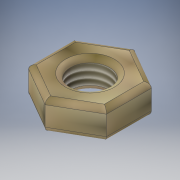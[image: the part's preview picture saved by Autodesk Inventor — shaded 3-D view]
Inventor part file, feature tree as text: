
AUTODESK INVENTOR PART (.ipt)
format: ipt  version: 2019 (Build 230136000, 136)  size: 160,768 bytes
history: native  units: mm
features: extrude x1, fillet x1, thread x1, sketch x1
ambient origin geometry x8: Origin, YZ Plane, XZ Plane, XY Plane, X Axis, Y Axis, Z Axis, Center Point
bodies: Solid1 (feature_tree)
feature tree (4):
  extrude  "Extrusion1"  Depth=3.0mm TaperAngle=0.0deg
  fillet  "Fillet1"  Radius=0.5mm
  thread  "Thread1"  [1 undecoded]
  sketch  "Sketch1"  dims[d0=4.0mm d1=3.0mm d2=0.0mm d3=0.5mm d4=4.0mm d5=10.0mm d6=0.0mm]
note: 1 required parameter value undecoded (feature->parameter linkage not recoverable at this tier; creation-order binding heuristic only, values carry confidence <= 0.55)
